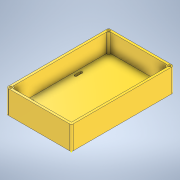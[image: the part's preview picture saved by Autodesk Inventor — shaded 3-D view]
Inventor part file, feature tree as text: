
AUTODESK INVENTOR PART (.ipt)
format: ipt  version: 2020 (Build 240168000, 168)  size: 267,776 bytes
history: native  units: mm
features: sketch x5, extrude x4, hole x1, fillet x1
ambient origin geometry x8: Origin, YZ Plane, XZ Plane, XY Plane, X Axis, Y Axis, Z Axis, Center Point
bodies: Solid1 (feature_tree)
feature tree (11):
  sketch  "Sketch1"  dims[d0=70.0mm d1=110.0mm]
  extrude  "Extrusion1"  Depth=110.0mm
  extrude  "Extrusion2"  Depth=105.0mm
  extrude  "Extrusion3"  Depth=52.5mm
  extrude  "Extrusion4"  Depth=16.21mm
  hole  "Hole1"  [1 undecoded]
  fillet  "Fillet2"  Radius=16.4mm
  sketch  "Sketch6"  dims[d8=3.0mm d9=2.5mm d10=16.4mm d11=3.55mm d12=3.0mm d13=2.5mm d14=19.89mm d15=16.4mm d16=3.9mm d17=16.21mm d18=16.4mm d19=3.55mm d20=3.0mm d21=2.5mm d22=3.0mm d23=2.5mm d24=25.0mm d25=0.0mm d26=5.0mm d27=0.0mm d28=3.0mm d29=4.0mm d30=3.0mm d31=4.0mm d32=3.0mm d33=4.0mm d34=3.0mm d35=90.0deg d36=4.0mm d37=1.0mm d38=0.0mm d40=5.0mm d41=24.0mm d42=0.0mm d43=3.0mm d44=6.0mm d45=3.5mm d46=2.0mm d47=90.0deg d48=40.0mm d49=20.594885mm d50=2.0mm]
  sketch  "Sketch2"  dims[d2=65.0mm d3=105.0mm]
  sketch  "Sketch3"  dims[d4=52.5mm d5=52.5mm]
  sketch  "Sketch5"  dims[d6=3.9mm d7=16.21mm]
note: 1 required parameter value undecoded (feature->parameter linkage not recoverable at this tier; creation-order binding heuristic only, values carry confidence <= 0.55)
